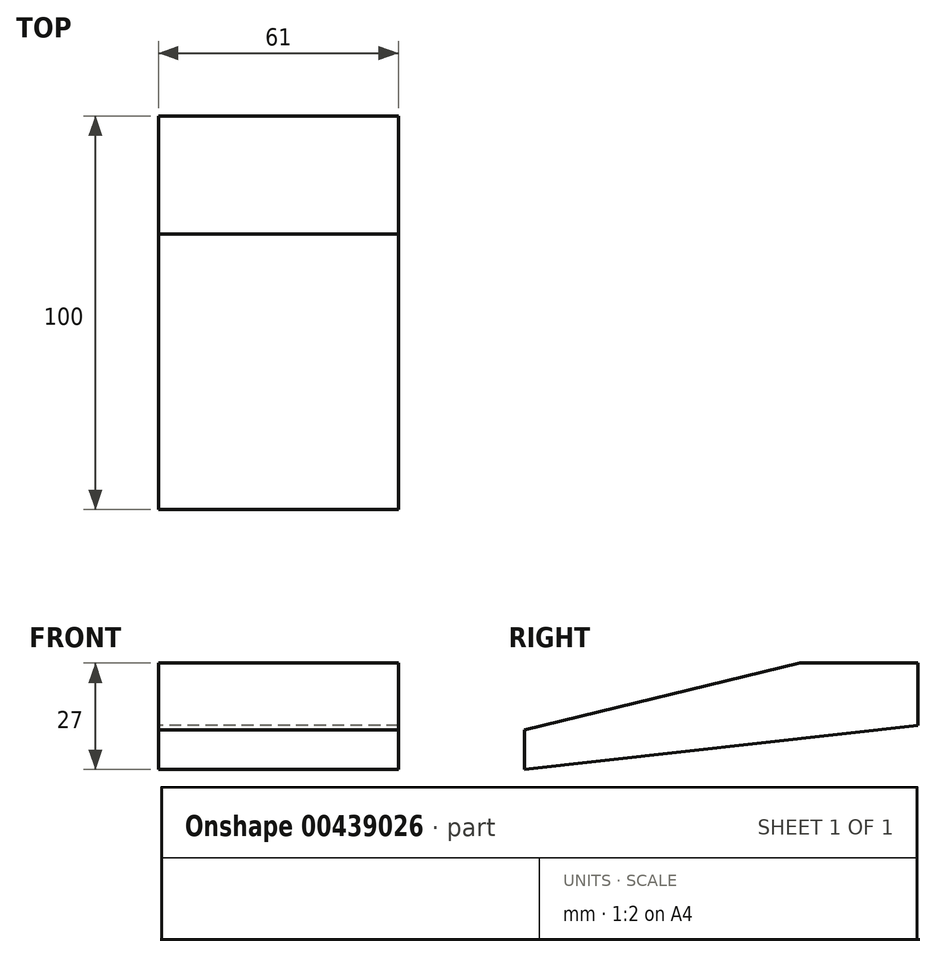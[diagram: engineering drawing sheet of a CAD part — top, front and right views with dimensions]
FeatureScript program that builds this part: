
annotation { "Feature Type Name" : "Feature", "Feature Type Description" : "" }
export const myFeature = defineFeature(function(context is Context, id is Id, definition is map)
    precondition{}
    {
        {
            var Q0;
            Q0=qCreatedBy(makeId("Right.planeOp"),FACE);
            var sketch = newSketch(context, id + "F0", { "sketchPlane" : qUnion([Q0])});
            skLineSegment(sketch, "E0", {"start": v(-70, 0) * mm, "end": v(30, 0) * mm});
            skLineSegment(sketch, "E1", {"start": v(30, 0) * mm, "end": v(-70, 0) * mm});
            skLineSegment(sketch, "E2", {"start": v(-70, 0) * mm, "end": v(-70, 5) * mm});
            skLineSegment(sketch, "E3", {"start": v(30, 0) * mm, "end": v(30, 5) * mm});
            skLineSegment(sketch, "E4", {"start": v(30, 5) * mm, "end": v(-70, 5) * mm});
            skPoint(sketch, "E5", {"position": v(-20, 0) * mm});
            skLineSegment(sketch, "E6", {"start": v(-70, 7) * mm, "end": v(-70, 17.09) * mm});
            skLineSegment(sketch, "E7", {"start": v(-70, 17.09) * mm, "end": v(-70, 17.09) * mm});
            skLineSegment(sketch, "E8", {"start": v(-70, 17.09) * mm, "end": v(0, 34) * mm});
            skLineSegment(sketch, "E9", {"start": v(0, 34) * mm, "end": v(0, 34) * mm});
            skLineSegment(sketch, "E10", {"start": v(30, 34) * mm, "end": v(0, 34) * mm});
            skLineSegment(sketch, "E11", {"start": v(30, 34) * mm, "end": v(30, 18.16) * mm});
            skLineSegment(sketch, "E12", {"start": v(30, 18.16) * mm, "end": v(-70, 7) * mm});
            skSolve(sketch);
        }
        {
            var Q0;
            Q0=makeQuery(id+"F0.imprint","IMPRINT",FACE,{"disambiguationData":[TD([[makeQuery(id+"F0.imprint","IMPRINT",EDGE,{"derivedFrom":sQuery(id+"F0.wireOp",EDGE,"E6")}),-1.0]])]});
            var Q1;
            Q1=makeQuery(id+"F0.imprint","IMPRINT",FACE,{"disambiguationData":[TD([[makeQuery(id+"F0.imprint","IMPRINT",EDGE,{"derivedFrom":sQuery(id+"F0.wireOp",EDGE,"E1")}),-1.0]])]});
            extrude(context, id + "F1", {"entities" : qUnion([Q0, Q1]), "depth" : 61 * mm});
        }
    });
